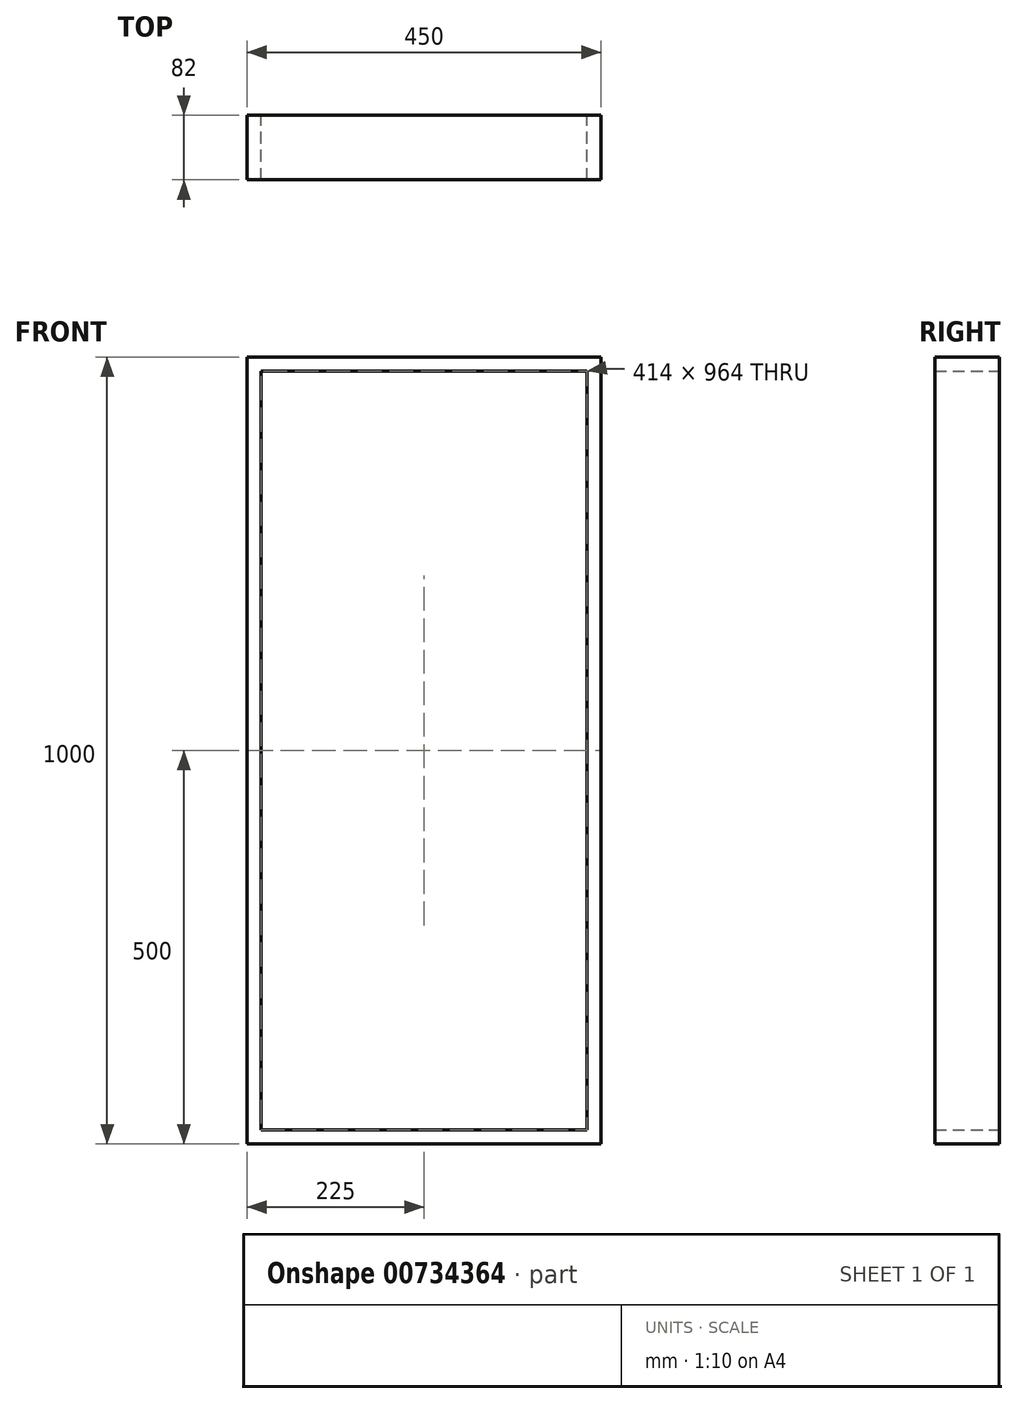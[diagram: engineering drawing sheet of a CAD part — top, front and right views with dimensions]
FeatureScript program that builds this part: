
annotation { "Feature Type Name" : "Feature", "Feature Type Description" : "" }
export const myFeature = defineFeature(function(context is Context, id is Id, definition is map)
    precondition{}
    {
        {
            var Q0;
            Q0=qCreatedBy(makeId("Front.planeOp"),FACE);
            var sketch = newSketch(context, id + "F0", { "sketchPlane" : qUnion([Q0])});
            skLineSegment(sketch, "E0.bottom", {"start": v(-225, 500) * mm, "end": v(225, 500) * mm});
            skLineSegment(sketch, "E0.top", {"start": v(-225, -500) * mm, "end": v(225, -500) * mm});
            skLineSegment(sketch, "E0.left", {"start": v(-225, 500) * mm, "end": v(-225, -500) * mm});
            skLineSegment(sketch, "E0.right", {"start": v(225, 500) * mm, "end": v(225, -500) * mm});
            skLineSegment(sketch, "E1", {"start": v(-225, 500) * mm, "end": v(225, -500) * mm, "construction": true});
            skLineSegment(sketch, "E2.bottom", {"start": v(207, 482) * mm, "end": v(-207, 482) * mm});
            skLineSegment(sketch, "E2.top", {"start": v(207, -482) * mm, "end": v(-207, -482) * mm});
            skLineSegment(sketch, "E2.left", {"start": v(207, 482) * mm, "end": v(207, -482) * mm});
            skLineSegment(sketch, "E2.right", {"start": v(-207, 482) * mm, "end": v(-207, -482) * mm});
            skPoint(sketch, "E2.middle", {"position": v(0, 0) * mm});
            skSolve(sketch);
        }
        {
            var Q0;
            Q0 = qSketchRegion(id + "F0", true);
            extrude(context, id + "F1", {"entities" : qUnion([Q0]), "depth" : 82 * mm, "offsetDistance" : 25 * mm});
        }
    });
